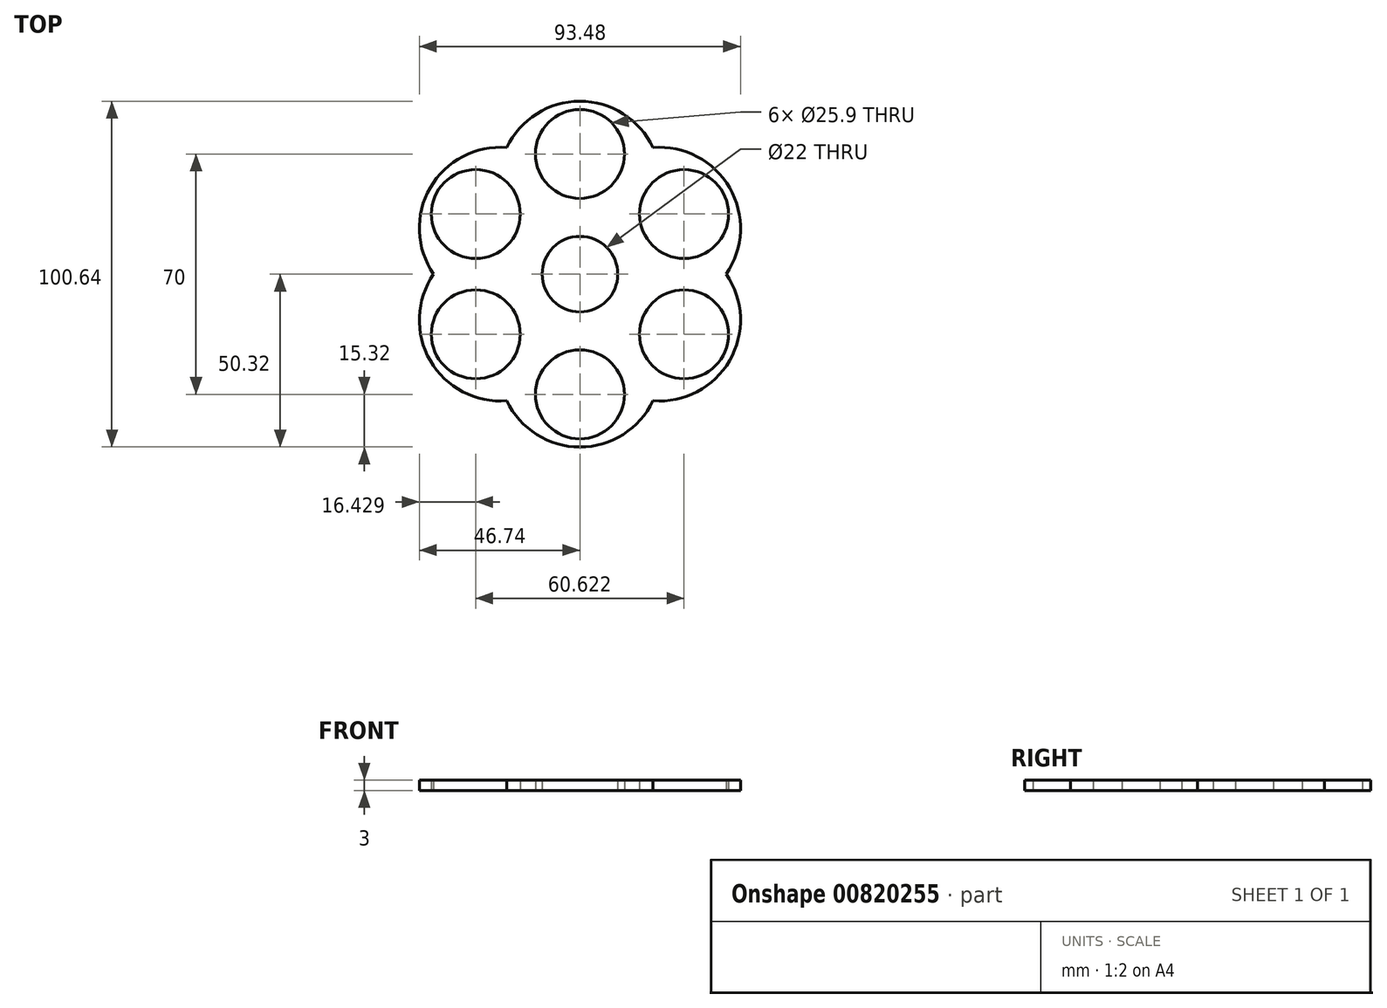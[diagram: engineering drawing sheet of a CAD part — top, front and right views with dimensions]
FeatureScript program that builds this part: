
annotation { "Feature Type Name" : "Feature", "Feature Type Description" : "" }
export const myFeature = defineFeature(function(context is Context, id is Id, definition is map)
    precondition{}
    {
        {
            var Q0;
            Q0=qCreatedBy(makeId("Top.planeOp"),FACE);
            var sketch = newSketch(context, id + "F0", { "sketchPlane" : qUnion([Q0])});
            skArc(sketch, "E0", {"start": v(9.65, 5.27) * mm, "mid": v(0, 11) * mm, "end": v(-9.65, 5.27) * mm});
            skCircle(sketch, "E1", {"center": v(0, 35) * mm, "radius": 12.95 * mm});
            skArc(sketch, "E2", {"start": v(21.28, 36.87) * mm, "mid": v(0, 50.32) * mm, "end": v(-21.28, 36.87) * mm});
            skArc(sketch, "E3.1.0", {"start": v(-21.28, 36.87) * mm, "mid": v(-43.58, 25.16) * mm, "end": v(-42.57, 0) * mm});
            skCircle(sketch, "E3.1.1", {"center": v(-30.31, 17.5) * mm, "radius": 12.95 * mm});
            skArc(sketch, "E3.1.2", {"start": v(0.26, 11) * mm, "mid": v(-9.53, 5.5) * mm, "end": v(-9.4, -5.72) * mm});
            skArc(sketch, "E3.2.0", {"start": v(-42.57, 0) * mm, "mid": v(-43.58, -25.16) * mm, "end": v(-21.28, -36.87) * mm});
            skCircle(sketch, "E3.2.1", {"center": v(-30.31, -17.5) * mm, "radius": 12.95 * mm});
            skArc(sketch, "E3.2.2", {"start": v(-9.4, 5.72) * mm, "mid": v(-9.53, -5.5) * mm, "end": v(0.26, -11) * mm});
            skArc(sketch, "E3.3.0", {"start": v(-21.28, -36.87) * mm, "mid": v(0, -50.32) * mm, "end": v(21.28, -36.87) * mm});
            skCircle(sketch, "E3.3.1", {"center": v(0, -35) * mm, "radius": 12.95 * mm});
            skArc(sketch, "E3.3.2", {"start": v(-9.65, -5.27) * mm, "mid": v(0, -11) * mm, "end": v(9.65, -5.27) * mm});
            skArc(sketch, "E3.4.0", {"start": v(21.28, -36.87) * mm, "mid": v(43.58, -25.16) * mm, "end": v(42.57, 0) * mm});
            skCircle(sketch, "E3.4.1", {"center": v(30.31, -17.5) * mm, "radius": 12.95 * mm});
            skArc(sketch, "E3.4.2", {"start": v(-0.26, -11) * mm, "mid": v(9.53, -5.5) * mm, "end": v(9.4, 5.72) * mm});
            skArc(sketch, "E3.5.0", {"start": v(42.57, 0) * mm, "mid": v(43.58, 25.16) * mm, "end": v(21.28, 36.87) * mm});
            skCircle(sketch, "E3.5.1", {"center": v(30.31, 17.5) * mm, "radius": 12.95 * mm});
            skArc(sketch, "E3.5.2", {"start": v(9.4, -5.72) * mm, "mid": v(9.53, 5.5) * mm, "end": v(-0.26, 11) * mm});
            skSolve(sketch);
        }
        {
            var Q0;
            Q0 = qSketchRegion(id + "F0", true);
            extrude(context, id + "F1", {"entities" : qUnion([Q0]), "depth" : 3 * mm, "offsetDistance" : 25 * mm});
        }
    });
